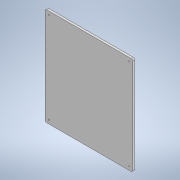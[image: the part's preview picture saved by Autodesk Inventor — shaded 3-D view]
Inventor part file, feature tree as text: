
AUTODESK INVENTOR PART (.ipt)
format: ipt  version: 2020.1 (Build 241239000, 239)  size: 116,736 bytes
history: native  units: mm
features: extrude x1, fillet x1, sketch x1
ambient origin geometry x8: Origin, YZ Plane, XZ Plane, XY Plane, X Axis, Y Axis, Z Axis, Center Point
bodies: Solid1 (feature_tree)
feature tree (3):
  extrude  "Extrusion1"  Depth=270.0mm
  fillet  "Fillet1"  Radius=10.0mm
  sketch  "Sketch1"  dims[d0=241.6mm d1=270.0mm d2=10.0mm d3=10.0mm d4=3.0mm d5=10.0mm d6=10.0mm d7=3.0mm d8=10.0mm d9=10.0mm d10=3.0mm d11=10.0mm d12=10.0mm d13=3.0mm d14=6.0mm d15=0.0mm d16=4.0mm]
